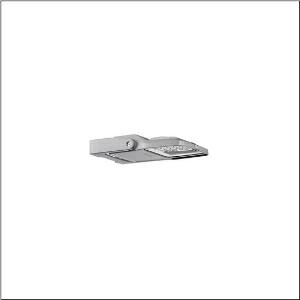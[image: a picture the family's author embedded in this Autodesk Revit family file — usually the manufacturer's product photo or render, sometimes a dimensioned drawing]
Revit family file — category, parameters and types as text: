
# Revit family: floodlight_fl_21_iq_micro___pl43_5xa7762a2a2a_df73
name_source: partatom
category: Lighting Fixtures
units: mm (PartAtom-declared; Revit-internal decimal feet)

## family parameters
Cut with Voids When Loaded = No
Host = Face
Light Source = No
Part Type = Normal
Room Calculation Point = No
Round Connector Dimension = Use Diameter
Shared = No

## types (1)
- --- (1 x LED, 3040 lm, 23.1 W, 3000K)
    Apparent Load = 23 VA
    CIE Flux Codes = 29 80 99 100 100
    Color Rendering = 70
    Color Temperature = 3000K
    Default Elevation = 1800 mm
    Description = Floodlight FL 21 iQ micro, floodlight, primary light control with lens, of PMMA, primary optical cover: protective disc, of toughened safety glass, transparent, light distribution: PL43, light emission: direct distribution, installation type: surface-mounted, LED, High Power LED, rated luminous flux: 3.040lm, luminous efficacy: 132lm/W, light colour: 730, colour temperature: 3000K, control: Auto-Match, Temp-Guard, Night-Set, Smart-Wire, Desk-Remote (wireless, voltage-free reading and setting of iQ features in the workshop via application-optimized NFC function/RFID function), optimised constant luminous flux control (CLO 2.0), Street-Remote, with terminal, 6-pole, mains connection: 220..240V, AC, 50/60Hz, start of lifetime: 23W, end of service life: 24W, reduction: 11W, luminaire housing, of diecast aluminium, powder-coated, Siteco® metallic grey (DB 702S), corrosivity category C5 mid according to DIN EN ISO 12944, sealing non-destructively replaceable, design bracket, of diecast aluminium, powder-coated, Siteco® metallic grey (DB 702S), protection rating (complete): IP66, insulation class (complete): insulation class II (safety insulation), certification: CE, ENEC, VDE, protection symbol: D, impact resistance: IK07, permissible operating ambient temperature: -40..+40°C, permissible operating ambient temperature for outdoor applications: -40..+50°C, standard: DIN EN 12944, LABS conformity tested according to VDMA 24364:2018-05, packaging unit: 1 piece

Light Distribution: PL43
    Height = 65 mm
    Lamp = 1 x LED
    Lamp Light Flux = 3040 lm
    Lamp Power = 23.1 W
    Lamp count = 1
    Length = 312 mm
    Luminous efficacy = 132 lm/W
    Manufacturer = Siteco
    ModVariant = No
    Model = 5XA7762A2A2A
    Mounting Place = Wall
    Mounting Type = Surface mounted
    Number of Poles = 1
    OnlyDefault = Yes
    Power Factor = 1
    Product Name = Floodlight FL 21 iQ micro | PL43
    Product group = floodlight | wall mounted
    ProductGroupID = 2001
    Protection Class = Protection class II
    Protection Degree = IP 66
    RLX_Detail_Level = 1
    RLX_Emergency_Light_Flux = 0 lm
    RLX_Emergency_Type = 0
    RLX_Emergency_Type_DB = No
    RlxData = <blob elided: 98325 chars, md5=a925c35a>
    Socket = socket
    Standby Power = 0 W
    System Light Flux = 3040 lm
    System Power = 23 W
    Type Comments = factory setting: luminous flux: 100 % | dim-lin: 254 | 455 mA
    Type Image = l_1006878.jpg
    URL = http://relux.com
    VarID = @adj_147875
    Voltage = 0 V
    Weight = 0.00 kg
    Width = 230 mm

## geometry (parser evidence)
native form markers: Blend x4, Sweep x13
no freeform markers — native parametric forms only
